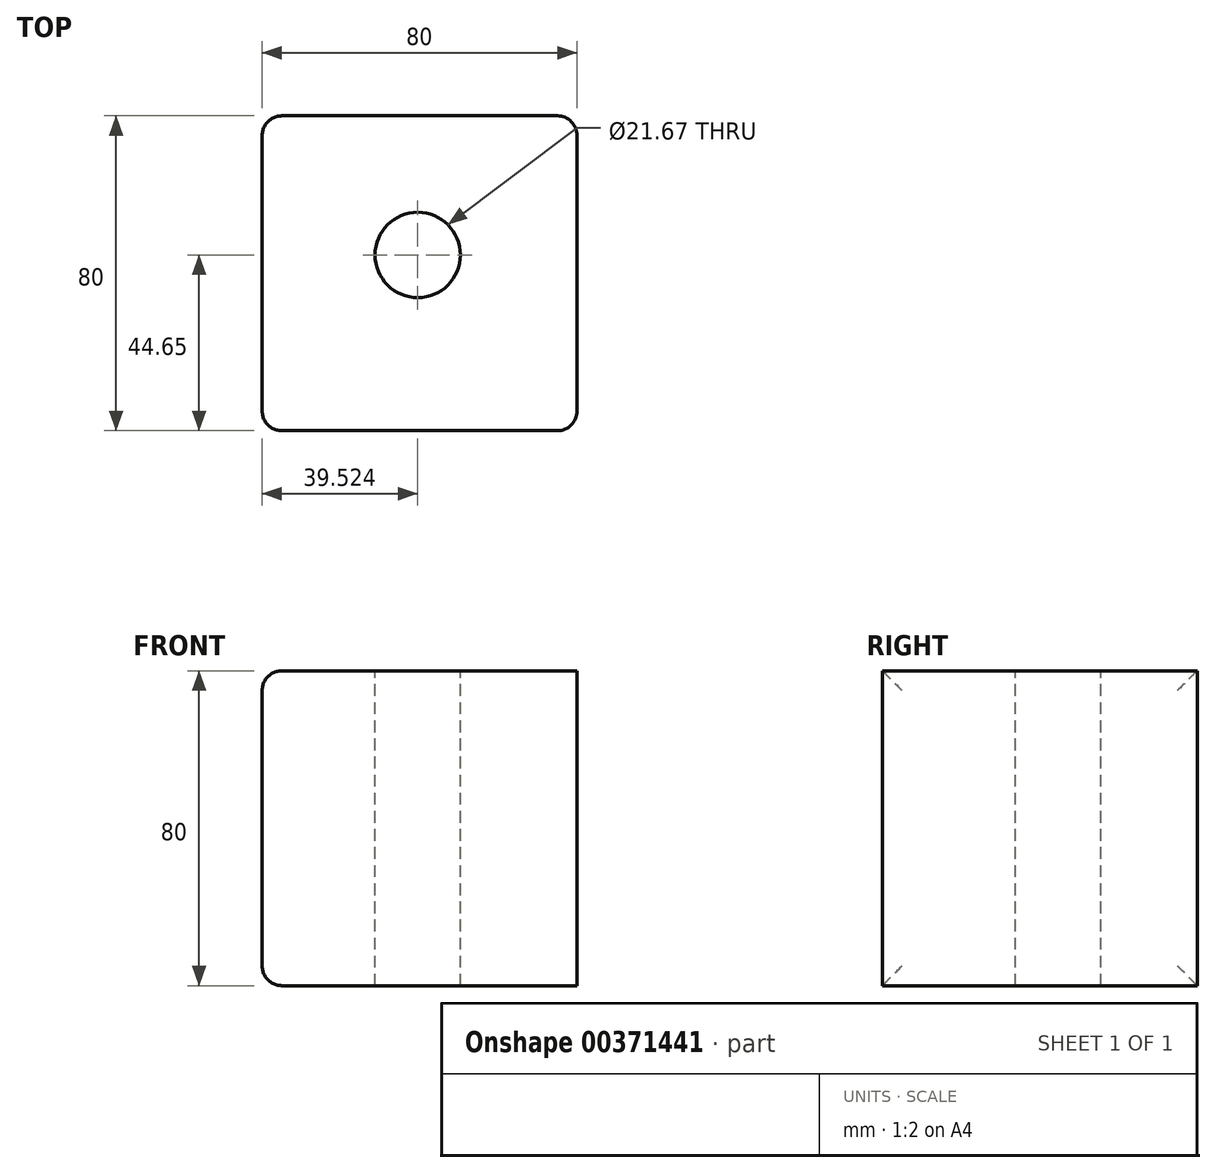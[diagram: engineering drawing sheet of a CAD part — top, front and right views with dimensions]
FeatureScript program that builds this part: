
annotation { "Feature Type Name" : "Feature", "Feature Type Description" : "" }
export const myFeature = defineFeature(function(context is Context, id is Id, definition is map)
    precondition{}
    {
        {
            var Q0;
            Q0=qCreatedBy(makeId("Top.planeOp"),FACE);
            var sketch = newSketch(context, id + "F0", { "sketchPlane" : qUnion([Q0])});
            skLineSegment(sketch, "E0.bottom", {"start": v(-81.45, 68.8) * mm, "end": v(-1.45, 68.8) * mm});
            skLineSegment(sketch, "E0.top", {"start": v(-81.45, -11.2) * mm, "end": v(-1.45, -11.2) * mm});
            skLineSegment(sketch, "E0.left", {"start": v(-81.45, 68.8) * mm, "end": v(-81.45, -11.2) * mm});
            skLineSegment(sketch, "E0.right", {"start": v(-1.45, 68.8) * mm, "end": v(-1.45, -11.2) * mm});
            skSolve(sketch);
        }
        {
            var Q0;
            Q0=makeQuery(id+"F0.imprint","IMPRINT",FACE,{"disambiguationData":[TD([[makeQuery(id+"F0.imprint","IMPRINT",EDGE,{"derivedFrom":sQuery(id+"F0.wireOp",EDGE,"E0.bottom")}),-1.0]])]});
            extrude(context, id + "F1", {"entities" : qUnion([Q0]), "depth" : 80 * mm});
        }
        {
            var Q0;
            Q0=makeQuery(id+"F1.opExtrude","CAP_FACE",FACE,{"disambiguationData":[OSD([sQuery(id+"F0.wireOp",EDGE,"E0.bottom"),sQuery(id+"F0.wireOp",EDGE,"E0.top"),sQuery(id+"F0.wireOp",EDGE,"E0.left"),sQuery(id+"F0.wireOp",EDGE,"E0.right")])],"isStart":false});
            var sketch = newSketch(context, id + "F2", { "sketchPlane" : qUnion([Q0])});
            skCircle(sketch, "E1", {"center": v(-41.93, 33.45) * mm, "radius": 10.84 * mm});
            skSolve(sketch);
        }
        {
            var Q0;
            Q0=makeQuery(id+"F0hT7hNh27IjyyS_1.opExtrude","CAP_EDGE",EDGE,{"disambiguationData":[OSD([sQuery(id+"F0.wireOp",EDGE,"E0.left")])],"isStart":false});
            var Q1;
            Q1=makeQuery(id+"F0hT7hNh27IjyyS_1.opExtrude","CAP_EDGE",EDGE,{"disambiguationData":[OSD([sQuery(id+"F0.wireOp",EDGE,"E0.bottom")])],"isStart":false});
            var Q2;
            Q2=makeQuery(id+"F0hT7hNh27IjyyS_1.opExtrude","CAP_EDGE",EDGE,{"disambiguationData":[OSD([sQuery(id+"F0.wireOp",EDGE,"E0.right")])],"isStart":false});
            var Q3;
            Q3=makeQuery(id+"F0hT7hNh27IjyyS_1.opExtrude","CAP_EDGE",EDGE,{"disambiguationData":[OSD([sQuery(id+"F0.wireOp",EDGE,"E0.top")])],"isStart":false});
            var Q4;
            {var subQ0=sQuery(id+"F0.wireOp",EDGE,"E0.right");var subQ1=sQuery(id+"F0.wireOp",EDGE,"E0.top");Q4=makeQuery(id+"F0hT7hNh27IjyyS_1.boolean.opBoolean","MERGE",EDGE,{"derivedFrom":[makeQuery(id+"F1.opExtrude","SWEPT_EDGE",EDGE,{"disambiguationData":[OSD([subQ1,subQ0])]}),makeQuery(id+"F0hT7hNh27IjyyS_1.opExtrude","SWEPT_EDGE",EDGE,{"disambiguationData":[OSD([subQ1,subQ0])]})]});}
            var Q5;
            {var subQ0=sQuery(id+"F0.wireOp",EDGE,"E0.right");var subQ1=sQuery(id+"F0.wireOp",EDGE,"E0.bottom");Q5=makeQuery(id+"F0hT7hNh27IjyyS_1.boolean.opBoolean","MERGE",EDGE,{"derivedFrom":[makeQuery(id+"F1.opExtrude","SWEPT_EDGE",EDGE,{"disambiguationData":[OSD([subQ1,subQ0])]}),makeQuery(id+"F0hT7hNh27IjyyS_1.opExtrude","SWEPT_EDGE",EDGE,{"disambiguationData":[OSD([subQ1,subQ0])]})]});}
            var Q6;
            {var subQ0=sQuery(id+"F0.wireOp",EDGE,"E0.left");var subQ1=sQuery(id+"F0.wireOp",EDGE,"E0.bottom");Q6=makeQuery(id+"F0hT7hNh27IjyyS_1.boolean.opBoolean","MERGE",EDGE,{"derivedFrom":[makeQuery(id+"F1.opExtrude","SWEPT_EDGE",EDGE,{"disambiguationData":[OSD([subQ1,subQ0])]}),makeQuery(id+"F0hT7hNh27IjyyS_1.opExtrude","SWEPT_EDGE",EDGE,{"disambiguationData":[OSD([subQ1,subQ0])]})]});}
            var Q7;
            {var subQ0=sQuery(id+"F0.wireOp",EDGE,"E0.left");Q7=makeQuery(id+"F0hT7hNh27IjyyS_1.boolean.opBoolean","MERGE",FACE,{"derivedFrom":[makeQuery(id+"F1.opExtrude","SWEPT_FACE",FACE,{"disambiguationData":[OSD([subQ0])]}),makeQuery(id+"F0hT7hNh27IjyyS_1.opExtrude","SWEPT_FACE",FACE,{"disambiguationData":[OSD([subQ0])]})]});}
            fillet(context, id + "F3", {"entities" : qUnion([Q0, Q1, Q2, Q3, Q4, Q5, Q6, Q7]), "radius" : 5 * mm, "tangentPropagation" : true, "allowEdgeOverflow" : false});
        }
        {
            var Q0;
            Q0=makeQuery(id+"F2.imprint","IMPRINT",FACE,{"disambiguationData":[TD([[makeQuery(id+"F2.imprint","IMPRINT",EDGE,{"derivedFrom":sQuery(id+"F2.wireOp",EDGE,"E1")}),1.0]])]});
            extrude(context, id + "F4", {"entities" : qUnion([Q0]), "operationType" : NewBodyOperationType.REMOVE, "endBound" : BoundingType.THROUGH_ALL, "oppositeDirection" : true, "depth" : 25 * mm});
        }
    });
